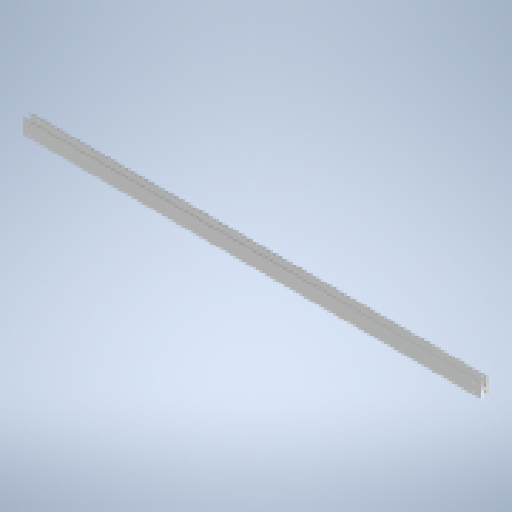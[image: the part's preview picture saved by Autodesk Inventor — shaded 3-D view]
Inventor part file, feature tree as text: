
AUTODESK INVENTOR PART (.ipt)
format: ipt  version: 2025 (Build 290162010, 162A)  size: 298,496 bytes
history: native  units: mm
features: sketch x2, other x1, extrude x1, hole x1
ambient origin geometry x8: Origin, YZ Plane, XZ Plane, XY Plane, X Axis, Y Axis, Z Axis, Center Point
bodies: Body1 (feature_tree)
feature tree (5):
  other  "Träger"
  extrude  "Extrusion1"  Depth=1.5mm
  hole  "Bohrung1"  [1 undecoded]
  sketch  "Skizze1"  dims[d0=2.0mm d1=1.5mm]
  sketch  "Skizze2"  dims[d2=32.0mm d3=18.0mm d4=1000.0mm d5=0.0mm d6=15.0mm d8=15.0mm d9=15.0mm d10=5.0mm d11=6.0mm d12=10.4mm d13=2.0mm d14=90.0deg d15=8.0mm d16=20.594885mm d17=8.5mm d18=15.0mm]
note: 1 required parameter value undecoded (feature->parameter linkage not recoverable at this tier; creation-order binding heuristic only, values carry confidence <= 0.55)
